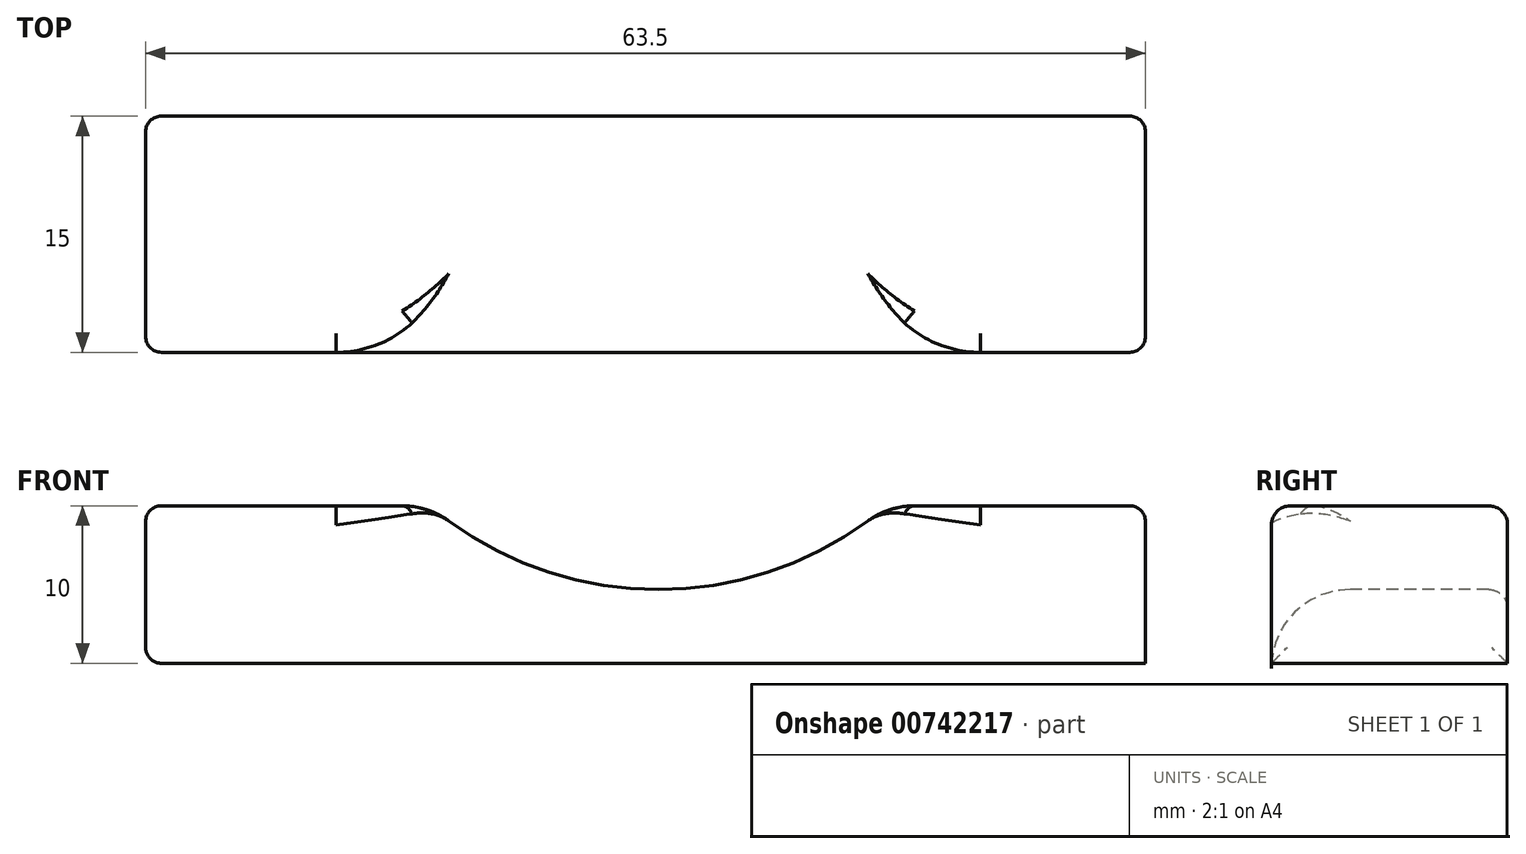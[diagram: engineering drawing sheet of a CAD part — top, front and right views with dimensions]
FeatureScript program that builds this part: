
annotation { "Feature Type Name" : "Feature", "Feature Type Description" : "" }
export const myFeature = defineFeature(function(context is Context, id is Id, definition is map)
    precondition{}
    {
        {
            var Q0;
            Q0=qCreatedBy(makeId("Top.planeOp"),FACE);
            var sketch = newSketch(context, id + "F0", { "sketchPlane" : qUnion([Q0])});
            skLineSegment(sketch, "E0.bottom", {"start": v(-18.03, 6.26) * mm, "end": v(45.47, 6.26) * mm});
            skLineSegment(sketch, "E0.top", {"start": v(-18.03, -8.74) * mm, "end": v(45.47, -8.74) * mm});
            skLineSegment(sketch, "E0.left", {"start": v(-18.03, 6.26) * mm, "end": v(-18.03, -8.74) * mm});
            skLineSegment(sketch, "E0.right", {"start": v(45.47, 6.26) * mm, "end": v(45.47, -8.74) * mm});
            skSolve(sketch);
        }
        {
            var Q0;
            Q0=makeQuery(id+"F0.imprint","IMPRINT",FACE,{"disambiguationData":[TD([[makeQuery(id+"F0.imprint","IMPRINT",EDGE,{"derivedFrom":sQuery(id+"F0.wireOp",EDGE,"E0.bottom")}),-1.0]])]});
            extrude(context, id + "F1", {"entities" : qUnion([Q0]), "depth" : 10 * mm, "offsetDistance" : 25 * mm});
        }
        {
            var Q0;
            Q0=makeQuery(id+"F1.opExtrude","SWEPT_FACE",FACE,{"disambiguationData":[OSD([sQuery(id+"F0.wireOp",EDGE,"E0.top")])]});
            var sketch = newSketch(context, id + "F2", { "sketchPlane" : qUnion([Q0])});
            skArc(sketch, "E1", {"start": v(0, 10) * mm, "mid": v(14.53, 4.69) * mm, "end": v(29.07, 10) * mm});
            skSolve(sketch);
        }
        {
            var Q0;
            {var subQ0=sQuery(id+"F2.wireOp",EDGE,"E1");Q0=makeQuery(id+"F2.imprint","IMPRINT",FACE,{"disambiguationData":[TD([[makeQuery(id+"F2.imprint","IMPRINT",EDGE,{"derivedFrom":subQ0}),1.0]])]});}
            extrude(context, id + "F3", {"entities" : qUnion([Q0]), "operationType" : NewBodyOperationType.REMOVE, "oppositeDirection" : true, "depth" : 25 * mm, "offsetDistance" : 25 * mm});
        }
        {
            var Q0;
            Q0=makeQuery(id+"F1.opExtrude","CAP_EDGE",EDGE,{"disambiguationData":[OSD([sQuery(id+"F0.wireOp",EDGE,"E0.right")])],"isStart":false});
            var Q1;
            Q1=makeQuery(id+"F1.opExtrude","SWEPT_FACE",FACE,{"disambiguationData":[OSD([sQuery(id+"F0.wireOp",EDGE,"E0.left")])]});
            var Q2;
            Q2=makeQuery(id+"F1.opExtrude","SWEPT_EDGE",EDGE,{"disambiguationData":[OSD([sQuery(id+"F0.wireOp",EDGE,"E0.bottom"),sQuery(id+"F0.wireOp",EDGE,"E0.right")])]});
            var Q3;
            Q3=makeQuery(id+"F1.opExtrude","SWEPT_EDGE",EDGE,{"disambiguationData":[OSD([sQuery(id+"F0.wireOp",EDGE,"E0.top"),sQuery(id+"F0.wireOp",EDGE,"E0.right")])]});
            fillet(context, id + "F4", {"entities" : qUnion([Q0, Q1, Q2, Q3]), "radius" : 1 * mm, "tangentPropagation" : true, "allowEdgeOverflow" : false});
        }
        {
            var Q0;
            Q0=makeQuery(id+"F3.boolean.opBoolean","COPY",EDGE,{"derivedFrom":makeQuery(id+"F3.opExtrude","CAP_EDGE",EDGE,{"disambiguationData":[OSD([sQuery(id+"F2.wireOp",EDGE,"E1")])],"isStart":true})});
            var Q1;
            {var subQ0=sQuery(id+"F0.wireOp",EDGE,"E0.left");var subQ1=sQuery(id+"F0.wireOp",EDGE,"E0.top");Q1=makeQuery(id+"F3.boolean.opBoolean","SPLIT",EDGE,{"disambiguationData":[TD([makeQuery(id+"F1.opExtrude","SWEPT_FACE",FACE,{"disambiguationData":[OSD([subQ0])]})])],"derivedFrom":makeQuery(id+"F1.opExtrude","CAP_EDGE",EDGE,{"disambiguationData":[OSD([subQ1])],"isStart":false})});}
            var Q2;
            {var subQ0=sQuery(id+"F0.wireOp",EDGE,"E0.right");var subQ1=sQuery(id+"F0.wireOp",EDGE,"E0.top");Q2=makeQuery(id+"F3.boolean.opBoolean","SPLIT",EDGE,{"disambiguationData":[TD([makeQuery(id+"F1.opExtrude","SWEPT_FACE",FACE,{"disambiguationData":[OSD([subQ0])]})])],"derivedFrom":makeQuery(id+"F1.opExtrude","CAP_EDGE",EDGE,{"disambiguationData":[OSD([subQ1])],"isStart":false})});}
            fillet(context, id + "F5", {"entities" : qUnion([Q0, Q1, Q2]), "radius" : 1.2 * mm, "tangentPropagation" : true, "allowEdgeOverflow" : false});
        }
        {
            var Q0;
            {var subQ0=sQuery(id+"F0.wireOp",EDGE,"E0.bottom");var subQ1=sQuery(id+"F0.wireOp",EDGE,"E0.right");Q0=makeQuery(id+"F3.boolean.opBoolean","SPLIT",EDGE,{"disambiguationData":[TD([makeQuery(id+"F1.opExtrude","SWEPT_FACE",FACE,{"disambiguationData":[OSD([subQ1])]})])],"derivedFrom":makeQuery(id+"F1.opExtrude","CAP_EDGE",EDGE,{"disambiguationData":[OSD([subQ0])],"isStart":false})});}
            var Q1;
            Q1=makeQuery(id+"F3.boolean.opBoolean","INTERSECT",EDGE,{"derivedFrom":[makeQuery(id+"F1.opExtrude","SWEPT_FACE",FACE,{"disambiguationData":[OSD([sQuery(id+"F0.wireOp",EDGE,"E0.bottom")])]}),makeQuery(id+"F3.opExtrude","SWEPT_FACE",FACE,{"disambiguationData":[OSD([sQuery(id+"F2.wireOp",EDGE,"E1")])]})]});
            var Q2;
            {var subQ0=sQuery(id+"F0.wireOp",EDGE,"E0.bottom");var subQ1=sQuery(id+"F0.wireOp",EDGE,"E0.left");Q2=makeQuery(id+"F3.boolean.opBoolean","SPLIT",EDGE,{"disambiguationData":[TD([makeQuery(id+"F1.opExtrude","SWEPT_FACE",FACE,{"disambiguationData":[OSD([subQ1])]})])],"derivedFrom":makeQuery(id+"F1.opExtrude","CAP_EDGE",EDGE,{"disambiguationData":[OSD([subQ0])],"isStart":false})});}
            fillet(context, id + "F6", {"entities" : qUnion([Q0, Q1, Q2]), "radius" : 1.2 * mm, "tangentPropagation" : true, "allowEdgeOverflow" : false});
        }
        {
            var Q0;
            {var subQ0=sQuery(id+"F2.wireOp",EDGE,"E1");var subQ1=sQuery(id+"F0.wireOp",EDGE,"E0.top");Q0=makeQuery(id+"F3.boolean.opBoolean","COPY",EDGE,{"derivedFrom":makeQuery(id+"F3.opExtrude","SWEPT_EDGE",EDGE,{"disambiguationData":[OSD([subQ1,subQ0]),TDD([makeQuery(id+"F2.imprint","INTERSECT",VERTEX,{"disambiguationData":[OD(1.0)],"derivedFrom":[makeQuery(id+"F1.opExtrude","CAP_EDGE",EDGE,{"disambiguationData":[OSD([subQ1])],"isStart":false}),subQ0]})])]})});}
            var Q1;
            {var subQ0=sQuery(id+"F2.wireOp",EDGE,"E1");var subQ1=sQuery(id+"F0.wireOp",EDGE,"E0.top");Q1=makeQuery(id+"F3.boolean.opBoolean","COPY",EDGE,{"derivedFrom":makeQuery(id+"F3.opExtrude","SWEPT_EDGE",EDGE,{"disambiguationData":[OSD([subQ1,subQ0]),TDD([makeQuery(id+"F2.imprint","INTERSECT",VERTEX,{"disambiguationData":[OD(0.0)],"derivedFrom":[makeQuery(id+"F1.opExtrude","CAP_EDGE",EDGE,{"disambiguationData":[OSD([subQ1])],"isStart":false}),subQ0]})])]})});}
            fillet(context, id + "F7", {"entities" : qUnion([Q0, Q1]), "radius" : 5 * mm, "tangentPropagation" : true, "allowEdgeOverflow" : false});
        }
    });
